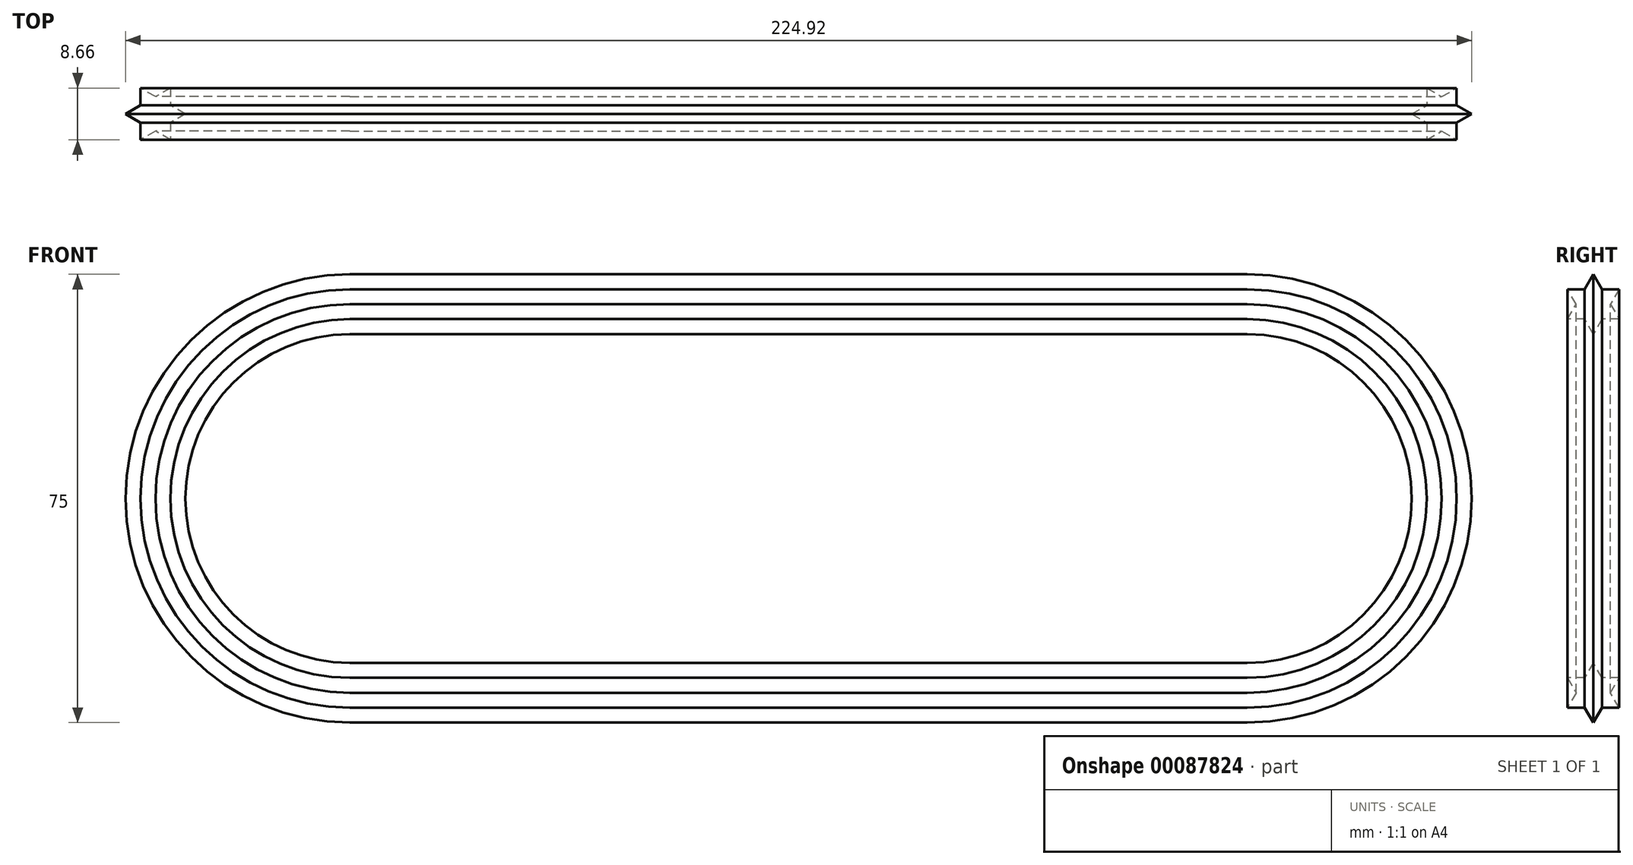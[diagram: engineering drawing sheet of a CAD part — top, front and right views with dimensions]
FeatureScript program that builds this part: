
annotation { "Feature Type Name" : "Feature", "Feature Type Description" : "" }
export const myFeature = defineFeature(function(context is Context, id is Id, definition is map)
    precondition{}
    {
        {
            var Q0;
            Q0=qCreatedBy(makeId("Front.planeOp"),FACE);
            var sketch = newSketch(context, id + "F0", { "sketchPlane" : qUnion([Q0])});
            skLineSegment(sketch, "E0", {"start": v(-75.83, 0) * mm, "end": v(74.09, 0) * mm});
            skArc(sketch, "E1.0.startCap", {"start": v(-75.83, -30) * mm, "mid": v(-105.83, 0) * mm, "end": v(-75.83, 30) * mm});
            skLineSegment(sketch, "E1.0.endCap", {"start": v(74.09, 30) * mm, "end": v(74.09, 30) * mm});
            skLineSegment(sketch, "E1.0.left", {"start": v(-75.83, 30) * mm, "end": v(-75.83, 30) * mm});
            skLineSegment(sketch, "E1.0.right", {"start": v(-75.83, -30) * mm, "end": v(-75.83, -30) * mm});
            skLineSegment(sketch, "E2", {"start": v(-75.83, 30) * mm, "end": v(74.09, 30) * mm});
            skLineSegment(sketch, "E3", {"start": v(-75.83, -30) * mm, "end": v(74.09, -30) * mm});
            skArc(sketch, "E4", {"start": v(74.09, 30) * mm, "mid": v(104.09, 0) * mm, "end": v(74.09, -30) * mm});
            skLineSegment(sketch, "E5", {"start": v(74.09, -30) * mm, "end": v(74.09, -30) * mm});
            skSolve(sketch);
        }
        {
            var Q0;
            Q0=qCreatedBy(makeId("Right.planeOp"),FACE);
            var Q1;
            Q1=sQuery(id+"F0.wireOp",VERTEX,"E4.start");
            cPlane(context, id + "F1", {"entities" : qUnion([Q0, Q1]), "cplaneType" : CPlaneType.PLANE_POINT, "offset" : 150 * mm, "width" : 150 * mm, "height" : 150 * mm});
        }
        {
            var Q0;
            Q0=qCreatedBy(id+"F1.planeOp",FACE);
            var sketch = newSketch(context, id + "F2", { "sketchPlane" : qUnion([Q0])});
            skCircle(sketch, "E6.cCircle", {"center": v(0, 32.5) * mm, "radius": 2.5 * mm, "construction": true});
            skLineSegment(sketch, "E6.0", {"start": v(4.33, 30) * mm, "end": v(-4.33, 30) * mm});
            skLineSegment(sketch, "E6.1", {"start": v(-4.33, 30) * mm, "end": v(0, 37.5) * mm});
            skLineSegment(sketch, "E6.2", {"start": v(0, 37.5) * mm, "end": v(4.33, 30) * mm});
            skPoint(sketch, "E6.0.midPoint", {"position": v(0, 30) * mm});
            skLineSegment(sketch, "E7.0", {"start": v(0, 27.5) * mm, "end": v(-4.33, 35) * mm});
            skLineSegment(sketch, "E7.1", {"start": v(-4.33, 35) * mm, "end": v(4.33, 35) * mm});
            skLineSegment(sketch, "E7.2", {"start": v(4.33, 35) * mm, "end": v(0, 27.5) * mm});
            skPoint(sketch, "E7.0.midPoint", {"position": v(-2.17, 31.25) * mm});
            skSolve(sketch);
        }
        {
            var Q0;
            {var subQ0=sQuery(id+"F2.wireOp",EDGE,"E7.1");var subQ1=sQuery(id+"F2.wireOp",EDGE,"E6.2");var subQ2=makeQuery(id+"F2.imprint","INTERSECT",VERTEX,{"derivedFrom":[subQ1,subQ0]});Q0=makeQuery(id+"F2.imprint","IMPRINT",FACE,{"disambiguationData":[TD([[makeQuery(id+"F2.imprint","IMPRINT",EDGE,{"disambiguationData":[TD([[subQ2,-1.0]])],"derivedFrom":subQ1}),1.0]])]});}
            var Q1;
            {var subQ0=sQuery(id+"F2.wireOp",EDGE,"E6.2");var subQ1=sQuery(id+"F2.wireOp",EDGE,"E6.1");var subQ2=makeQuery(id+"F2.imprint","INTERSECT",VERTEX,{"derivedFrom":[subQ1,subQ0]});Q1=makeQuery(id+"F2.imprint","IMPRINT",FACE,{"disambiguationData":[TD([[makeQuery(id+"F2.imprint","IMPRINT",EDGE,{"disambiguationData":[TD([[subQ2,1.0]])],"derivedFrom":subQ1}),-1.0]])]});}
            var Q2;
            {var subQ0=sQuery(id+"F2.wireOp",EDGE,"E7.0");var subQ1=sQuery(id+"F2.wireOp",EDGE,"E6.1");var subQ2=makeQuery(id+"F2.imprint","INTERSECT",VERTEX,{"derivedFrom":[subQ1,subQ0]});Q2=makeQuery(id+"F2.imprint","IMPRINT",FACE,{"disambiguationData":[TD([[makeQuery(id+"F2.imprint","IMPRINT",EDGE,{"disambiguationData":[TD([[subQ2,-1.0]])],"derivedFrom":subQ1}),1.0]])]});}
            var Q3;
            {var subQ0=sQuery(id+"F2.wireOp",EDGE,"E6.1");var subQ1=sQuery(id+"F2.wireOp",EDGE,"E6.0");var subQ2=makeQuery(id+"F2.imprint","INTERSECT",VERTEX,{"derivedFrom":[subQ1,subQ0]});Q3=makeQuery(id+"F2.imprint","IMPRINT",FACE,{"disambiguationData":[TD([[makeQuery(id+"F2.imprint","IMPRINT",EDGE,{"disambiguationData":[TD([[subQ2,1.0]])],"derivedFrom":subQ1}),-1.0]])]});}
            var Q4;
            {var subQ0=sQuery(id+"F2.wireOp",EDGE,"E7.2");var subQ1=sQuery(id+"F2.wireOp",EDGE,"E6.0");var subQ2=makeQuery(id+"F2.imprint","INTERSECT",VERTEX,{"derivedFrom":[subQ1,subQ0]});Q4=makeQuery(id+"F2.imprint","IMPRINT",FACE,{"disambiguationData":[TD([[makeQuery(id+"F2.imprint","IMPRINT",EDGE,{"disambiguationData":[TD([[subQ2,-1.0]])],"derivedFrom":subQ1}),1.0]])]});}
            var Q5;
            {var subQ0=sQuery(id+"F2.wireOp",EDGE,"E6.2");var subQ1=sQuery(id+"F2.wireOp",EDGE,"E6.0");var subQ2=makeQuery(id+"F2.imprint","INTERSECT",VERTEX,{"derivedFrom":[subQ1,subQ0]});Q5=makeQuery(id+"F2.imprint","IMPRINT",FACE,{"disambiguationData":[TD([[makeQuery(id+"F2.imprint","IMPRINT",EDGE,{"disambiguationData":[TD([[subQ2,-1.0]])],"derivedFrom":subQ1}),-1.0]])]});}
            var Q6;
            {var subQ3=sQuery(id+"F2.wireOp",EDGE,"E7.2");var subQ9=sQuery(id+"F2.wireOp",EDGE,"E6.0");var subQ11=makeQuery(id+"F2.imprint","INTERSECT",VERTEX,{"derivedFrom":[subQ9,subQ3]});Q6=makeQuery(id+"F2.imprint","IMPRINT",FACE,{"disambiguationData":[TD([[makeQuery(id+"F2.imprint","IMPRINT",EDGE,{"disambiguationData":[TD([[subQ11,-1.0]])],"derivedFrom":subQ9}),-1.0]])]});}
            var Q7;
            Q7=sQuery(id+"F0.wireOp",EDGE,"E2");
            var Q8;
            Q8=sQuery(id+"F0.wireOp",EDGE,"E4");
            var Q9;
            Q9=sQuery(id+"F0.wireOp",EDGE,"E1.0.startCap");
            var Q10;
            Q10=sQuery(id+"F0.wireOp",EDGE,"E3");
            sweep(context, id + "F3", {"profiles" : qUnion([Q0, Q1, Q2, Q3, Q4, Q5, Q6]), "path" : qUnion([Q7, Q8, Q9, Q10])});
        }
    });
